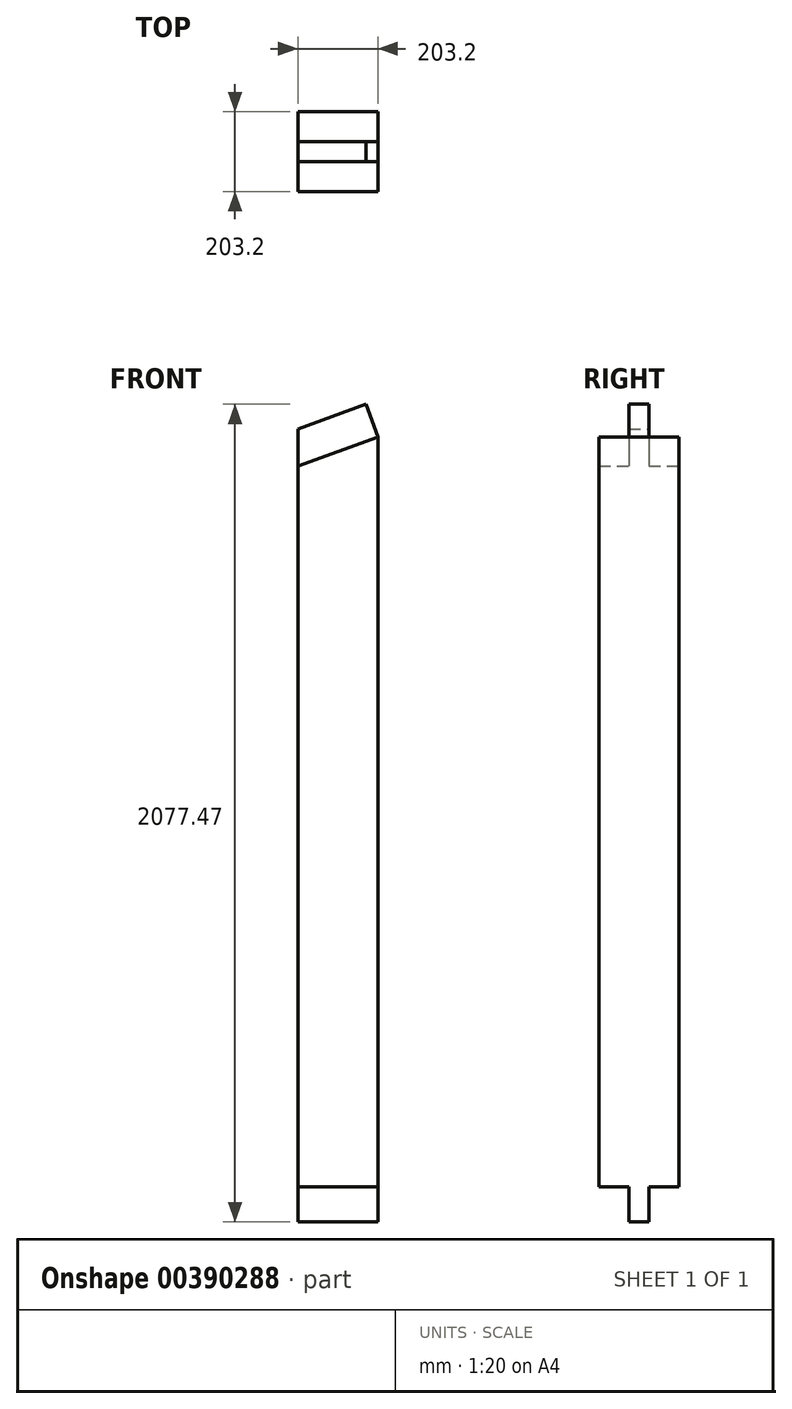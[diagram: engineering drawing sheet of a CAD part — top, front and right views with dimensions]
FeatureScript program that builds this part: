
annotation { "Feature Type Name" : "Feature", "Feature Type Description" : "" }
export const myFeature = defineFeature(function(context is Context, id is Id, definition is map)
    precondition{}
    {
        {
            var Q0;
            Q0=qCreatedBy(makeId("Front.planeOp"),FACE);
            var sketch = newSketch(context, id + "F0", { "sketchPlane" : qUnion([Q0])});
            skLineSegment(sketch, "E0.bottom", {"start": v(-101.6, 1003.3) * mm, "end": v(101.6, 1003.3) * mm});
            skLineSegment(sketch, "E0.top", {"start": v(-101.6, -1003.3) * mm, "end": v(101.6, -1003.3) * mm});
            skLineSegment(sketch, "E0.left", {"start": v(-101.6, 1003.3) * mm, "end": v(-101.6, -1003.3) * mm});
            skLineSegment(sketch, "E0.right", {"start": v(101.6, 1003.3) * mm, "end": v(101.6, -1003.3) * mm});
            skPoint(sketch, "E0.middle", {"position": v(0, 0) * mm});
            skLineSegment(sketch, "E1", {"start": v(101.6, 901.7) * mm, "end": v(-101.6, 827.99) * mm});
            skLineSegment(sketch, "E2", {"start": v(101.6, 901.7) * mm, "end": v(71.28, 985.27) * mm});
            skLineSegment(sketch, "E3", {"start": v(71.28, 985.27) * mm, "end": v(-101.6, 922.56) * mm});
            skLineSegment(sketch, "E4.top", {"start": v(-101.6, -1092.2) * mm, "end": v(101.6, -1092.2) * mm});
            skLineSegment(sketch, "E4.left", {"start": v(-101.6, -1003.3) * mm, "end": v(-101.6, -1092.2) * mm});
            skLineSegment(sketch, "E4.right", {"start": v(101.6, -1003.3) * mm, "end": v(101.6, -1092.2) * mm});
            skSolve(sketch);
        }
        {
            var Q0;
            {var subQ2=sQuery(id+"F0.wireOp",EDGE,"E1");Q0=makeQuery(id+"F0.imprint","IMPRINT",FACE,{"disambiguationData":[TD([[makeQuery(id+"F0.imprint","IMPRINT",EDGE,{"derivedFrom":subQ2}),1.0]])]});}
            extrude(context, id + "F1", {"entities" : qUnion([Q0]), "endBound" : BoundingType.SYMMETRIC, "depth" : 203.2 * mm});
        }
        {
            var Q0;
            {var subQ0=sQuery(id+"F0.wireOp",EDGE,"E1");Q0=makeQuery(id+"F0.imprint","IMPRINT",FACE,{"disambiguationData":[TD([[makeQuery(id+"F0.imprint","IMPRINT",EDGE,{"derivedFrom":subQ0}),-1.0]])]});}
            var Q1;
            Q1=makeQuery(id+"F0.imprint","IMPRINT",FACE,{"disambiguationData":[TD([[makeQuery(id+"F0.imprint","IMPRINT",EDGE,{"derivedFrom":sQuery(id+"F0.wireOp",EDGE,"E0.top")}),-1.0]])]});
            extrude(context, id + "F2", {"entities" : qUnion([Q0, Q1]), "operationType" : NewBodyOperationType.ADD, "endBound" : BoundingType.SYMMETRIC, "depth" : 50.8 * mm});
        }
    });
